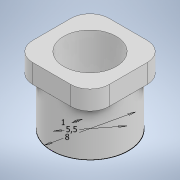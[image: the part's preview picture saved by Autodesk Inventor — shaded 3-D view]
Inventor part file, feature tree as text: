
AUTODESK INVENTOR PART (.ipt)
format: ipt  version: 2021 (Build 250183000, 183)  size: 140,288 bytes
history: native  units: mm
features: extrude x3, sketch x2, fillet x1
ambient origin geometry x8: Origin, YZ Plane, XZ Plane, XY Plane, X Axis, Y Axis, Z Axis, Center Point
bodies: Solide1 (feature_tree)
feature tree (6):
  sketch  "Esquisse1"
  extrude  "Extrusion1"  Depth=8.0mm
  extrude  "Extrusion2"  Depth=5.5mm
  extrude  "Extrusion3"  Depth=1.0mm
  fillet  "Congé1"  Radius=2.0mm
  sketch  "Esquisse2"
